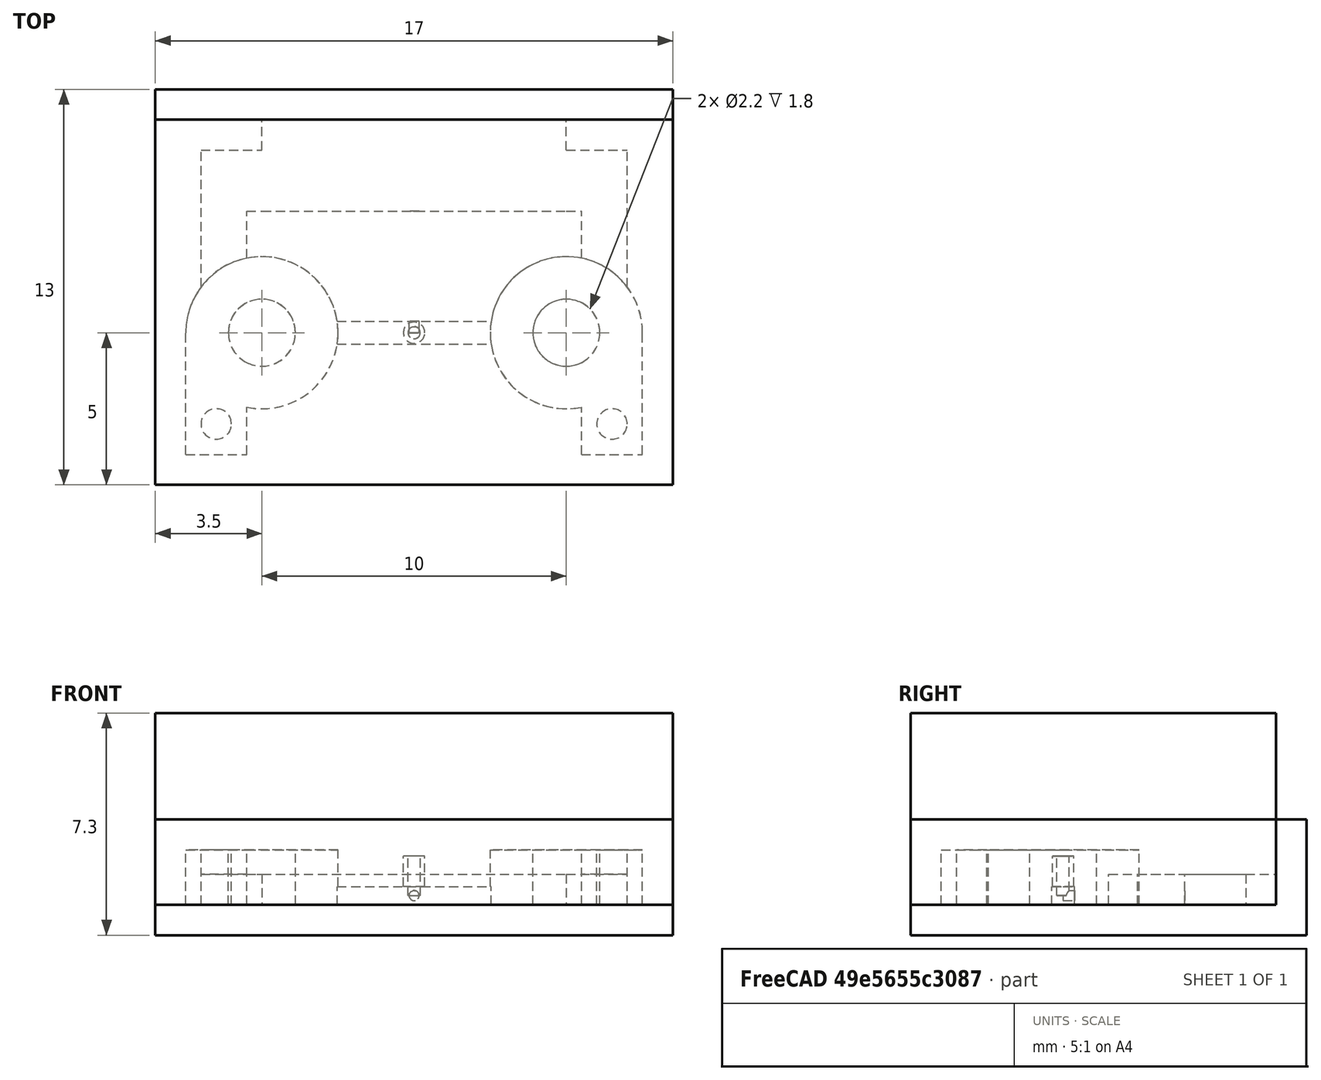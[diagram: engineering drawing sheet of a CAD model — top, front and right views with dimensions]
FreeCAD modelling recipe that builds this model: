
FCSTD DOCUMENT  (FreeCAD 0.18R16033 (Git))
Label: bowtie_prototype_1_milling
License: All rights reserved
LicenseURL: http://en.wikipedia.org/wiki/All_rights_reserved
objects: Path::FeaturePython×5, Part::FeaturePython×4, Part::Feature×2, App::FeaturePython×2, App::DocumentObjectGroup×2, Path::FeatureCompoundPython×2
note: 7 computed .brp shape members not serialized (recipe doc carries the construction recipe); baked Part::Feature solids carry a one-line shape summary decoded from their .brp

FEATURE [Part::Feature] Part__Feature  label="Fusion004"
  Placement = pos=(0,0,0.3) rot=(0,0,1;0rad)
  shape: bbox 15 x 11 x 1.8 mm, 64 faces (baked)
FEATURE [App::FeaturePython] SetupSheet  # Path/CAM operation (typed FeaturePython)
  ClearanceHeightExpression = OpStockZMax+SetupSheet.ClearanceHeightOffset
  ClearanceHeightOffset = 5
  FinalDepthExpression = OpFinalDepth
  HorizRapid = 0
  SafeHeightExpression = OpStockZMax+SetupSheet.SafeHeightOffset
  SafeHeightOffset = 3
  StartDepthExpression = OpStartDepth
  StepDownExpression = OpToolDiameter
  VertRapid = 0
FEATURE [Part::FeaturePython] Clone  label="Model-Fusion004"  # Draft clone (typed FeaturePython)
  AttacherType = Attacher::AttachEngine3D
  Fuse = false
  Objects = -> [Part__Feature]
  PathResource = Model
  Placement = pos=(0,0,0.3) rot=(0,0,1;0rad)
  Scale = (1,1,1)
FEATURE [App::DocumentObjectGroup] Model
  Group = -> [Clone]
FEATURE [Path::FeaturePython] T3__063_End_Mill  label="T3: 063 End Mill"  # Path/CAM operation (typed FeaturePython)
  HorizFeed = 11
  HorizRapid = 0
  SpindleDir = 0
  SpindleSpeed = 24000
  ToolNumber = 3
  VertFeed = 1
  VertRapid = 0
  expr: HorizRapid = SetupSheet.HorizRapid
  expr: VertRapid = SetupSheet.VertRapid
FEATURE [Path::FeaturePython] MillFace  # Path/CAM operation (typed FeaturePython)
  Active = true
  AreaParams:
    OpenMode = 0
    Angle = 45.0
    MinArcPoints = 4
    Coplanar = 0
    Tolerance = 1e-07
    CleanDistance = 0.0
    PocketExtraOffset = -1.0
    RoundPrecision = 0.0
    AngleShift = 0.0
    SubjectFill = 0
    PocketMode = 1
    PocketLastStepover = 0.0
    Simplify = False
    SectionTolerance = 1e-06
    MaxArcPoints = 100
    Offset = 0.0
    Accuracy = 0.01
    LastStepover = 0.0
    PocketStepover = 0.79
    ClipFill = 0
    ToolRadius = 0.79
    Outline = False
    ClipperScale = 10000000.0
    FromCenter = True
    Explode = False
    EndType = 0
    Shift = 0.0
    ExtraPass = 0
    Project = False
    JoinType = 0
    Thicken = False
    Stepdown = 1.0
    SectionMode = 2
    MiterLimit = 2.0
    Deflection = 0.01
    Reorient = True
    FitArcs = True
    SectionCount = -1
    SectionOffset = 0.0
    Stepover = 0.0
    Unit = 1.0
    Fill = 0
  Base = -> [Clone]
  BoundaryShape = 2
  ClearanceHeight = 11.3
  CutMode = 0
  ExtraOffset = 1
  FinalDepth = 1.8
  FinishDepth = 0
  KeepToolDown = false
  MinTravel = false
  OffsetPattern = 0
  OpFinalDepth = 1.8
  OpStartDepth = 6.3
  OpStockZMax = 6.3
  OpStockZMin = 0
  OpToolDiameter = 1.58
  PathParams = {'resume_height': 9.3, 'feedrate': 11.0, 'verbose': True, 'orientation': 1, 'return_end': True, 'preamble': False, 'retraction': 11.3, 'feedrate_v': 1.0}
  SafeHeight = 9.3
  StartAt = 0
  StartDepth = 6.3
  StartPoint = (0,0,0)
  StepDown = 1
  StepOver = 50
  ToolController = -> T3__063_End_Mill
  UseStartPoint = false
  ZigZagAngle = 45
  expr: ClearanceHeight = OpStockZMax + SetupSheet.ClearanceHeightOffset
  expr: SafeHeight = OpStockZMax + SetupSheet.SafeHeightOffset
  expr: StepDown = 1
  expr: FinalDepth = OpFinalDepth
  expr: StartDepth = OpStartDepth
FEATURE [Path::FeatureCompoundPython] Operations  # Path/CAM operation (typed FeaturePython)
  Group = -> [MillFace]
  UsePlacements = false
FEATURE [Path::FeatureCompoundPython] Operations001  # Path/CAM operation (typed FeaturePython)
  UsePlacements = false
FEATURE [App::FeaturePython] SetupSheet001  # Path/CAM operation (typed FeaturePython)
  ClearanceHeightExpression = OpStockZMax+SetupSheet001.ClearanceHeightOffset
  ClearanceHeightOffset = 5
  FinalDepthExpression = OpFinalDepth
  HorizRapid = 0
  SafeHeightExpression = OpStockZMax+SetupSheet001.SafeHeightOffset
  SafeHeightOffset = 3
  StartDepthExpression = OpStartDepth
  StepDownExpression = OpToolDiameter
  VertRapid = 0
FEATURE [Part::FeaturePython] Clone001  label="Model-Fusion005"  # Draft clone (typed FeaturePython)
  AttacherType = Attacher::AttachEngine3D
  Fuse = false
  Objects = -> [Part__Feature]
  PathResource = Model
  Placement = pos=(0,0,0.3) rot=(0,0,1;0rad)
  Scale = (1,1,1)
FEATURE [App::DocumentObjectGroup] Model001
  Group = -> [Clone001]
FEATURE [Part::FeaturePython] Stock001  # WARN: FeaturePython — macro-defined, semantics opaque (R4)
  Base = -> Model001
  ExtXneg = 1
  ExtXpos = 1
  ExtYneg = 1
  ExtYpos = 1
  ExtZneg = 1
  ExtZpos = 1
  Placement = pos=(-7.5,-4,0) rot=(0,0,1;0rad)
  StockType = FromBase
FEATURE [Path::FeaturePython] T1__125_End_Mill  label="T1: 125 End Mill"  # Path/CAM operation (typed FeaturePython)
  HorizFeed = 10
  HorizRapid = 0
  SpindleDir = 0
  SpindleSpeed = 24000
  ToolNumber = 1
  VertFeed = 0.3
  VertRapid = 0
  expr: HorizRapid = SetupSheet001.HorizRapid
  expr: VertRapid = SetupSheet001.VertRapid
FEATURE [Path::FeaturePython] Job001  label="Drill"  # Path/CAM operation (typed FeaturePython)
  GeometryTolerance = 0.01
  Model = -> Model001
  Operations = -> Operations001
  PostProcessor = 1
  SetupSheet = -> SetupSheet001
  Stock = -> Stock001
  ToolController = -> [T1__125_End_Mill]
FEATURE [Part::Feature] Part__Feature001  label="Fusion005"
  Placement = pos=(0,0,0.3) rot=(0,0,1;0rad)
  shape: bbox 15 x 11 x 1.8 mm, 64 faces (baked)
FEATURE [Part::FeaturePython] Stock002  # WARN: FeaturePython — macro-defined, semantics opaque (R4)
  Base = -> Model
  ExtXneg = 1
  ExtXpos = 1
  ExtYneg = 1
  ExtYpos = 0
  ExtZneg = 0
  ExtZpos = 4.5
  Placement = pos=(-7.5,-4,0) rot=(0,0,1;0rad)
  StockType = FromBase
FEATURE [Path::FeaturePython] Job  # Path/CAM operation (typed FeaturePython)
  GeometryTolerance = 0.01
  Model = -> Model
  Operations = -> Operations
  PostProcessor = 7
  PostProcessorOutputFile = <userpath>/NAS/primary_a/Projects/ion_printer/files/ionprinter/mechanical/GCode/bowtie_prototype_1
  SetupSheet = -> SetupSheet
  Stock = -> Stock002
  ToolController = -> [T3__063_End_Mill]
